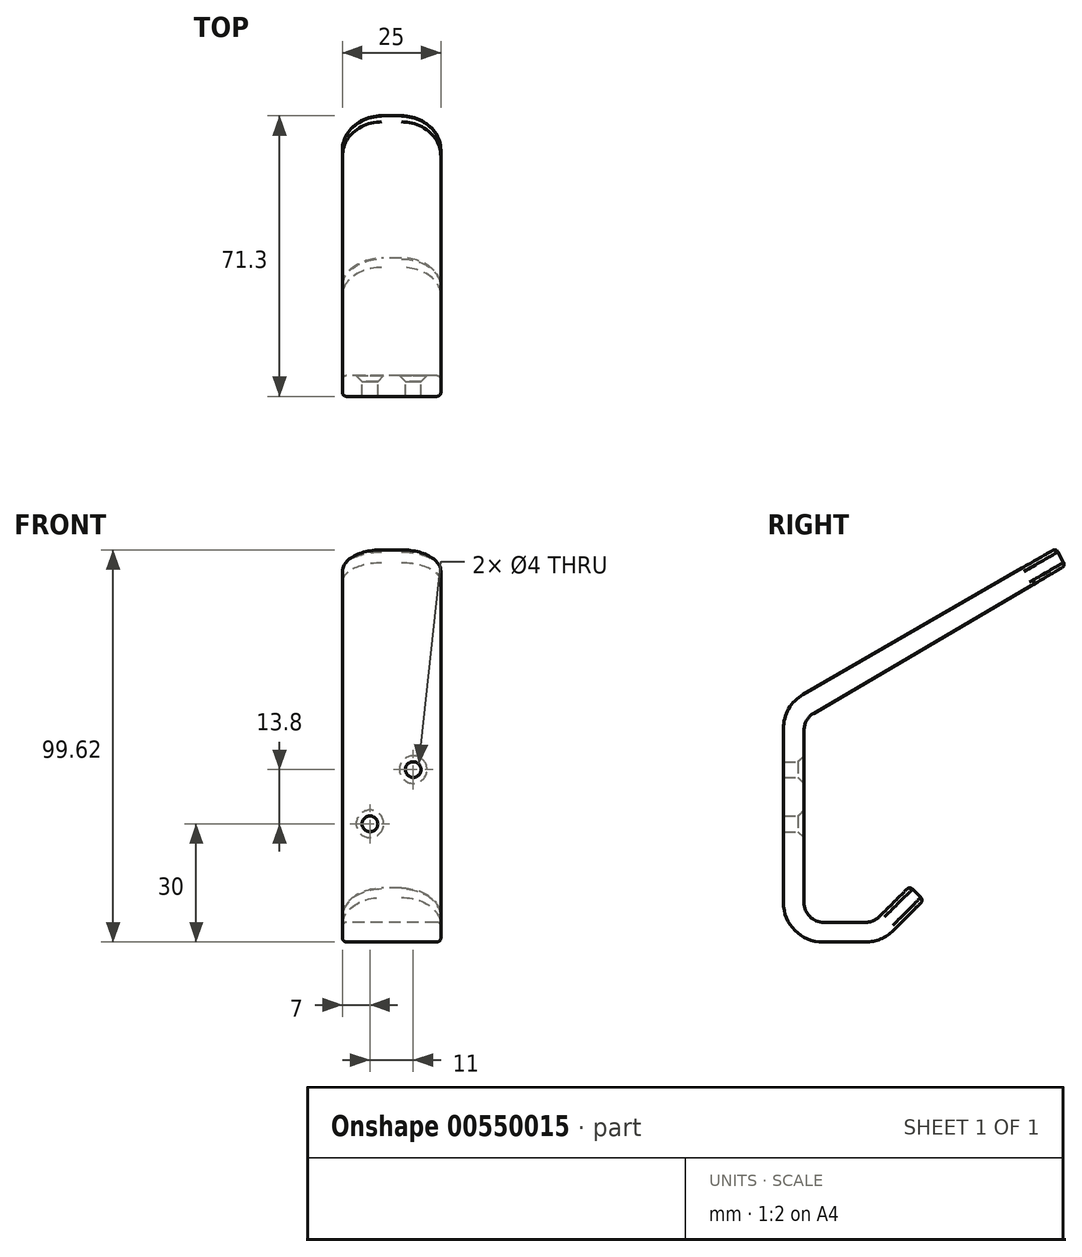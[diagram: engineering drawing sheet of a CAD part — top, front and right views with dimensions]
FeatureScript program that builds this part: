
annotation { "Feature Type Name" : "Feature", "Feature Type Description" : "" }
export const myFeature = defineFeature(function(context is Context, id is Id, definition is map)
    precondition{}
    {
        {
            var Q0;
            Q0=qCreatedBy(makeId("Right.planeOp"),FACE);
            var sketch = newSketch(context, id + "F0", { "sketchPlane" : qUnion([Q0])});
            skLineSegment(sketch, "E0", {"start": v(0, 0) * mm, "end": v(-25, 0) * mm});
            skLineSegment(sketch, "E1", {"start": v(-25, 0) * mm, "end": v(-25, 60) * mm});
            skLineSegment(sketch, "E2", {"start": v(-25, 60) * mm, "end": v(44.28, 100) * mm});
            skLineSegment(sketch, "E3", {"start": v(0, 0) * mm, "end": v(10.6, 10.6) * mm});
            skLineSegment(sketch, "E4", {"start": v(10.6, 10.6) * mm, "end": v(7.07, 14.14) * mm});
            skLineSegment(sketch, "E5", {"start": v(7.07, 14.14) * mm, "end": v(-2.07, 5) * mm});
            skLineSegment(sketch, "E6", {"start": v(-2.07, 5) * mm, "end": v(-19.76, 5) * mm});
            skLineSegment(sketch, "E7", {"start": v(-19.76, 6.6) * mm, "end": v(-19.76, 5) * mm});
            skLineSegment(sketch, "E8", {"start": v(-19.76, 5) * mm, "end": v(-19.76, 56.67) * mm});
            skLineSegment(sketch, "E9", {"start": v(-15.64, 59.09) * mm, "end": v(-19.76, 56.67) * mm});
            skLineSegment(sketch, "E10", {"start": v(-19.76, 56.67) * mm, "end": v(46.64, 95.6) * mm});
            skLineSegment(sketch, "E11", {"start": v(44.28, 100) * mm, "end": v(46.64, 95.6) * mm});
            skSolve(sketch);
        }
        {
            var Q0;
            Q0 = qSketchRegion(id + "F0", true);
            extrude(context, id + "F1", {"entities" : qUnion([Q0]), "depth" : 25 * mm, "offsetDistance" : 25 * mm});
        }
        {
            var Q0;
            Q0=makeQuery(id+"F1.opExtrude","SWEPT_EDGE",EDGE,{"disambiguationData":[OSD([sQuery(id+"F0.wireOp",EDGE,"E8"),sQuery(id+"F0.wireOp",EDGE,"E10")])]});
            var Q1;
            Q1=makeQuery(id+"F1.opExtrude","SWEPT_EDGE",EDGE,{"disambiguationData":[OSD([sQuery(id+"F0.wireOp",EDGE,"E6"),sQuery(id+"F0.wireOp",EDGE,"E8")])]});
            var Q2;
            Q2=makeQuery(id+"F1.opExtrude","SWEPT_EDGE",EDGE,{"disambiguationData":[OSD([sQuery(id+"F0.wireOp",EDGE,"E5"),sQuery(id+"F0.wireOp",EDGE,"E6")])]});
            fillet(context, id + "F2", {"entities" : qUnion([Q0, Q1, Q2]), "radius" : 5 * mm, "tangentPropagation" : true, "allowEdgeOverflow" : false});
        }
        {
            var Q0;
            Q0=makeQuery(id+"F1.opExtrude","SWEPT_EDGE",EDGE,{"disambiguationData":[OSD([sQuery(id+"F0.wireOp",EDGE,"E1"),sQuery(id+"F0.wireOp",EDGE,"E2")])]});
            var Q1;
            Q1=makeQuery(id+"F1.opExtrude","SWEPT_EDGE",EDGE,{"disambiguationData":[OSD([sQuery(id+"F0.wireOp",EDGE,"E0"),sQuery(id+"F0.wireOp",EDGE,"E1")])]});
            var Q2;
            Q2=makeQuery(id+"F1.opExtrude","SWEPT_EDGE",EDGE,{"disambiguationData":[OSD([sQuery(id+"F0.wireOp",EDGE,"E0"),sQuery(id+"F0.wireOp",EDGE,"E3")])]});
            fillet(context, id + "F3", {"entities" : qUnion([Q0, Q1, Q2]), "radius" : 10 * mm, "tangentPropagation" : true, "allowEdgeOverflow" : false});
        }
        {
            var Q0;
            Q0=makeQuery(id+"F1.opExtrude","CAP_EDGE",EDGE,{"disambiguationData":[OSD([sQuery(id+"F0.wireOp",EDGE,"E4")])],"isStart":false});
            var Q1;
            Q1=makeQuery(id+"F1.opExtrude","CAP_EDGE",EDGE,{"disambiguationData":[OSD([sQuery(id+"F0.wireOp",EDGE,"E4")])],"isStart":true});
            fillet(context, id + "F4", {"entities" : qUnion([Q0, Q1]), "radius" : 10 * mm, "tangentPropagation" : true, "allowEdgeOverflow" : false});
        }
        {
            var Q0;
            Q0=makeQuery(id+"F1.opExtrude","CAP_EDGE",EDGE,{"disambiguationData":[OSD([sQuery(id+"F0.wireOp",EDGE,"E11")])],"isStart":false});
            var Q1;
            Q1=makeQuery(id+"F1.opExtrude","CAP_EDGE",EDGE,{"disambiguationData":[OSD([sQuery(id+"F0.wireOp",EDGE,"E11")])],"isStart":true});
            fillet(context, id + "F5", {"entities" : qUnion([Q0, Q1]), "radius" : 10 * mm, "tangentPropagation" : true, "allowEdgeOverflow" : false});
        }
        {
            var Q0;
            Q0=makeQuery(id+"F1.opExtrude","CAP_EDGE",EDGE,{"disambiguationData":[OSD([sQuery(id+"F0.wireOp",EDGE,"E8")])],"isStart":false});
            var Q1;
            Q1=makeQuery(id+"F1.opExtrude","CAP_EDGE",EDGE,{"disambiguationData":[OSD([sQuery(id+"F0.wireOp",EDGE,"E10")])],"isStart":false});
            var Q2;
            {var subQ0=sQuery(id+"F0.wireOp",EDGE,"E10");var subQ1=sQuery(id+"F0.wireOp",EDGE,"E8");Q2=makeQuery(id+"F2.opFillet","BLEND_EDGE",EDGE,{"blendedFrom":[makeQuery(id+"F1.opExtrude","SWEPT_EDGE",EDGE,{"disambiguationData":[OSD([subQ1,subQ0])]}),makeQuery(id+"F1.opExtrude","CAP_FACE",FACE,{"disambiguationData":[OSD([sQuery(id+"F0.wireOp",EDGE,"E0"),sQuery(id+"F0.wireOp",EDGE,"E1"),sQuery(id+"F0.wireOp",EDGE,"E2"),sQuery(id+"F0.wireOp",EDGE,"E3"),sQuery(id+"F0.wireOp",EDGE,"E4"),sQuery(id+"F0.wireOp",EDGE,"E5"),sQuery(id+"F0.wireOp",EDGE,"E6"),subQ1,subQ0,sQuery(id+"F0.wireOp",EDGE,"E11")])],"isStart":false})],"blendedInto":[makeQuery(id+"F1.opExtrude","CAP_FACE",FACE,{"disambiguationData":[OSD([sQuery(id+"F0.wireOp",EDGE,"E0"),sQuery(id+"F0.wireOp",EDGE,"E1"),sQuery(id+"F0.wireOp",EDGE,"E2"),sQuery(id+"F0.wireOp",EDGE,"E3"),sQuery(id+"F0.wireOp",EDGE,"E4"),sQuery(id+"F0.wireOp",EDGE,"E5"),sQuery(id+"F0.wireOp",EDGE,"E6"),subQ1,subQ0,sQuery(id+"F0.wireOp",EDGE,"E11")])],"isStart":false})]});}
            var Q3;
            Q3=makeQuery(id+"F5.opFillet","BLEND_EDGE",EDGE,{"blendedFrom":[makeQuery(id+"F1.opExtrude","CAP_EDGE",EDGE,{"disambiguationData":[OSD([sQuery(id+"F0.wireOp",EDGE,"E11")])],"isStart":false}),makeQuery(id+"F1.opExtrude","SWEPT_FACE",FACE,{"disambiguationData":[OSD([sQuery(id+"F0.wireOp",EDGE,"E10")])]})],"blendedInto":[makeQuery(id+"F1.opExtrude","SWEPT_FACE",FACE,{"disambiguationData":[OSD([sQuery(id+"F0.wireOp",EDGE,"E10")])]})]});
            var Q4;
            Q4=makeQuery(id+"F1.opExtrude","SWEPT_EDGE",EDGE,{"disambiguationData":[OSD([sQuery(id+"F0.wireOp",EDGE,"E10"),sQuery(id+"F0.wireOp",EDGE,"E11")])]});
            var Q5;
            Q5=makeQuery(id+"F5.opFillet","BLEND_EDGE",EDGE,{"blendedFrom":[makeQuery(id+"F1.opExtrude","CAP_EDGE",EDGE,{"disambiguationData":[OSD([sQuery(id+"F0.wireOp",EDGE,"E11")])],"isStart":true}),makeQuery(id+"F1.opExtrude","SWEPT_FACE",FACE,{"disambiguationData":[OSD([sQuery(id+"F0.wireOp",EDGE,"E10")])]})],"blendedInto":[makeQuery(id+"F1.opExtrude","SWEPT_FACE",FACE,{"disambiguationData":[OSD([sQuery(id+"F0.wireOp",EDGE,"E10")])]})]});
            var Q6;
            Q6=makeQuery(id+"F1.opExtrude","CAP_EDGE",EDGE,{"disambiguationData":[OSD([sQuery(id+"F0.wireOp",EDGE,"E10")])],"isStart":true});
            var Q7;
            {var subQ0=sQuery(id+"F0.wireOp",EDGE,"E10");var subQ1=sQuery(id+"F0.wireOp",EDGE,"E8");Q7=makeQuery(id+"F2.opFillet","BLEND_EDGE",EDGE,{"blendedFrom":[makeQuery(id+"F1.opExtrude","SWEPT_EDGE",EDGE,{"disambiguationData":[OSD([subQ1,subQ0])]}),makeQuery(id+"F1.opExtrude","CAP_FACE",FACE,{"disambiguationData":[OSD([sQuery(id+"F0.wireOp",EDGE,"E0"),sQuery(id+"F0.wireOp",EDGE,"E1"),sQuery(id+"F0.wireOp",EDGE,"E2"),sQuery(id+"F0.wireOp",EDGE,"E3"),sQuery(id+"F0.wireOp",EDGE,"E4"),sQuery(id+"F0.wireOp",EDGE,"E5"),sQuery(id+"F0.wireOp",EDGE,"E6"),subQ1,subQ0,sQuery(id+"F0.wireOp",EDGE,"E11")])],"isStart":true})],"blendedInto":[makeQuery(id+"F1.opExtrude","CAP_FACE",FACE,{"disambiguationData":[OSD([sQuery(id+"F0.wireOp",EDGE,"E0"),sQuery(id+"F0.wireOp",EDGE,"E1"),sQuery(id+"F0.wireOp",EDGE,"E2"),sQuery(id+"F0.wireOp",EDGE,"E3"),sQuery(id+"F0.wireOp",EDGE,"E4"),sQuery(id+"F0.wireOp",EDGE,"E5"),sQuery(id+"F0.wireOp",EDGE,"E6"),subQ1,subQ0,sQuery(id+"F0.wireOp",EDGE,"E11")])],"isStart":true})]});}
            var Q8;
            Q8=makeQuery(id+"F1.opExtrude","CAP_EDGE",EDGE,{"disambiguationData":[OSD([sQuery(id+"F0.wireOp",EDGE,"E8")])],"isStart":true});
            fillet(context, id + "F6", {"entities" : qUnion([Q0, Q1, Q2, Q3, Q4, Q5, Q6, Q7, Q8]), "radius" : 1 * mm, "tangentPropagation" : true, "allowEdgeOverflow" : false});
        }
        {
            var Q0;
            Q0=makeQuery(id+"F1.opExtrude","SWEPT_FACE",FACE,{"disambiguationData":[OSD([sQuery(id+"F0.wireOp",EDGE,"E8")])]});
            var sketch = newSketch(context, id + "F7", { "sketchPlane" : qUnion([Q0])});
            skPoint(sketch, "E12", {"position": v(-18, 43.8) * mm});
            skPoint(sketch, "E13", {"position": v(-7, 30) * mm});
            skSolve(sketch);
        }
        {
            var Q0;
            Q0=sQuery(id+"F7.wireOp",VERTEX,"E12");
            var Q1;
            Q1=sQuery(id+"F7.wireOp",VERTEX,"E13");
            var Q2;
            Q2=makeQuery(id+"F1.opExtrude","SWEPT_BODY",BODY,{"disambiguationData":[OSD([sQuery(id+"F0.wireOp",EDGE,"E0"),sQuery(id+"F0.wireOp",EDGE,"E1"),sQuery(id+"F0.wireOp",EDGE,"E2"),sQuery(id+"F0.wireOp",EDGE,"E3"),sQuery(id+"F0.wireOp",EDGE,"E4"),sQuery(id+"F0.wireOp",EDGE,"E5"),sQuery(id+"F0.wireOp",EDGE,"E6"),sQuery(id+"F0.wireOp",EDGE,"E8"),sQuery(id+"F0.wireOp",EDGE,"E10"),sQuery(id+"F0.wireOp",EDGE,"E11")])]});
            hole(context, id + "F8", {"style" : HoleStyle.C_SINK, "endStyle" : HoleEndStyle.THROUGH, "holeDiameter" : 4 * mm, "cSinkDiameter" : 7 * mm, "cSinkAngle" : 90 * degree, "isTappedThrough" : true, "tappedDepth" : 12 * mm, "tapClearance" : 3, "locations" : qUnion([Q0, Q1]), "scope" : qUnion([Q2])});
        }
        {
            var Q0;
            Q0=makeQuery(id+"F4.opFillet","BLEND_EDGE",EDGE,{"blendedFrom":[makeQuery(id+"F1.opExtrude","CAP_EDGE",EDGE,{"disambiguationData":[OSD([sQuery(id+"F0.wireOp",EDGE,"E4")])],"isStart":false}),makeQuery(id+"F1.opExtrude","SWEPT_FACE",FACE,{"disambiguationData":[OSD([sQuery(id+"F0.wireOp",EDGE,"E3")])]})],"blendedInto":[makeQuery(id+"F1.opExtrude","SWEPT_FACE",FACE,{"disambiguationData":[OSD([sQuery(id+"F0.wireOp",EDGE,"E3")])]})]});
            var Q1;
            Q1=makeQuery(id+"F1.opExtrude","SWEPT_EDGE",EDGE,{"disambiguationData":[OSD([sQuery(id+"F0.wireOp",EDGE,"E3"),sQuery(id+"F0.wireOp",EDGE,"E4")])]});
            var Q2;
            Q2=makeQuery(id+"F4.opFillet","BLEND_EDGE",EDGE,{"blendedFrom":[makeQuery(id+"F1.opExtrude","CAP_EDGE",EDGE,{"disambiguationData":[OSD([sQuery(id+"F0.wireOp",EDGE,"E4")])],"isStart":true}),makeQuery(id+"F1.opExtrude","SWEPT_FACE",FACE,{"disambiguationData":[OSD([sQuery(id+"F0.wireOp",EDGE,"E3")])]})],"blendedInto":[makeQuery(id+"F1.opExtrude","SWEPT_FACE",FACE,{"disambiguationData":[OSD([sQuery(id+"F0.wireOp",EDGE,"E3")])]})]});
            var Q3;
            {var subQ0=sQuery(id+"F0.wireOp",EDGE,"E3");var subQ1=sQuery(id+"F0.wireOp",EDGE,"E0");Q3=makeQuery(id+"F3.opFillet","BLEND_EDGE",EDGE,{"blendedFrom":[makeQuery(id+"F1.opExtrude","SWEPT_EDGE",EDGE,{"disambiguationData":[OSD([subQ1,subQ0])]}),makeQuery(id+"F1.opExtrude","CAP_FACE",FACE,{"disambiguationData":[OSD([subQ1,sQuery(id+"F0.wireOp",EDGE,"E1"),sQuery(id+"F0.wireOp",EDGE,"E2"),subQ0,sQuery(id+"F0.wireOp",EDGE,"E4"),sQuery(id+"F0.wireOp",EDGE,"E5"),sQuery(id+"F0.wireOp",EDGE,"E6"),sQuery(id+"F0.wireOp",EDGE,"E8"),sQuery(id+"F0.wireOp",EDGE,"E10"),sQuery(id+"F0.wireOp",EDGE,"E11")])],"isStart":true})],"blendedInto":[makeQuery(id+"F1.opExtrude","CAP_FACE",FACE,{"disambiguationData":[OSD([subQ1,sQuery(id+"F0.wireOp",EDGE,"E1"),sQuery(id+"F0.wireOp",EDGE,"E2"),subQ0,sQuery(id+"F0.wireOp",EDGE,"E4"),sQuery(id+"F0.wireOp",EDGE,"E5"),sQuery(id+"F0.wireOp",EDGE,"E6"),sQuery(id+"F0.wireOp",EDGE,"E8"),sQuery(id+"F0.wireOp",EDGE,"E10"),sQuery(id+"F0.wireOp",EDGE,"E11")])],"isStart":true})]});}
            var Q4;
            Q4=makeQuery(id+"F1.opExtrude","CAP_EDGE",EDGE,{"disambiguationData":[OSD([sQuery(id+"F0.wireOp",EDGE,"E3")])],"isStart":true});
            var Q5;
            Q5=makeQuery(id+"F1.opExtrude","CAP_EDGE",EDGE,{"disambiguationData":[OSD([sQuery(id+"F0.wireOp",EDGE,"E0")])],"isStart":true});
            var Q6;
            {var subQ0=sQuery(id+"F0.wireOp",EDGE,"E3");var subQ1=sQuery(id+"F0.wireOp",EDGE,"E0");Q6=makeQuery(id+"F3.opFillet","BLEND_EDGE",EDGE,{"blendedFrom":[makeQuery(id+"F1.opExtrude","SWEPT_EDGE",EDGE,{"disambiguationData":[OSD([subQ1,subQ0])]}),makeQuery(id+"F1.opExtrude","CAP_FACE",FACE,{"disambiguationData":[OSD([subQ1,sQuery(id+"F0.wireOp",EDGE,"E1"),sQuery(id+"F0.wireOp",EDGE,"E2"),subQ0,sQuery(id+"F0.wireOp",EDGE,"E4"),sQuery(id+"F0.wireOp",EDGE,"E5"),sQuery(id+"F0.wireOp",EDGE,"E6"),sQuery(id+"F0.wireOp",EDGE,"E8"),sQuery(id+"F0.wireOp",EDGE,"E10"),sQuery(id+"F0.wireOp",EDGE,"E11")])],"isStart":false})],"blendedInto":[makeQuery(id+"F1.opExtrude","CAP_FACE",FACE,{"disambiguationData":[OSD([subQ1,sQuery(id+"F0.wireOp",EDGE,"E1"),sQuery(id+"F0.wireOp",EDGE,"E2"),subQ0,sQuery(id+"F0.wireOp",EDGE,"E4"),sQuery(id+"F0.wireOp",EDGE,"E5"),sQuery(id+"F0.wireOp",EDGE,"E6"),sQuery(id+"F0.wireOp",EDGE,"E8"),sQuery(id+"F0.wireOp",EDGE,"E10"),sQuery(id+"F0.wireOp",EDGE,"E11")])],"isStart":false})]});}
            var Q7;
            Q7=makeQuery(id+"F1.opExtrude","CAP_EDGE",EDGE,{"disambiguationData":[OSD([sQuery(id+"F0.wireOp",EDGE,"E3")])],"isStart":false});
            var Q8;
            Q8=makeQuery(id+"F1.opExtrude","CAP_EDGE",EDGE,{"disambiguationData":[OSD([sQuery(id+"F0.wireOp",EDGE,"E0")])],"isStart":false});
            var Q9;
            {var subQ0=sQuery(id+"F0.wireOp",EDGE,"E1");var subQ1=sQuery(id+"F0.wireOp",EDGE,"E0");Q9=makeQuery(id+"F3.opFillet","BLEND_EDGE",EDGE,{"blendedFrom":[makeQuery(id+"F1.opExtrude","SWEPT_EDGE",EDGE,{"disambiguationData":[OSD([subQ1,subQ0])]}),makeQuery(id+"F1.opExtrude","CAP_FACE",FACE,{"disambiguationData":[OSD([subQ1,subQ0,sQuery(id+"F0.wireOp",EDGE,"E2"),sQuery(id+"F0.wireOp",EDGE,"E3"),sQuery(id+"F0.wireOp",EDGE,"E4"),sQuery(id+"F0.wireOp",EDGE,"E5"),sQuery(id+"F0.wireOp",EDGE,"E6"),sQuery(id+"F0.wireOp",EDGE,"E8"),sQuery(id+"F0.wireOp",EDGE,"E10"),sQuery(id+"F0.wireOp",EDGE,"E11")])],"isStart":false})],"blendedInto":[makeQuery(id+"F1.opExtrude","CAP_FACE",FACE,{"disambiguationData":[OSD([subQ1,subQ0,sQuery(id+"F0.wireOp",EDGE,"E2"),sQuery(id+"F0.wireOp",EDGE,"E3"),sQuery(id+"F0.wireOp",EDGE,"E4"),sQuery(id+"F0.wireOp",EDGE,"E5"),sQuery(id+"F0.wireOp",EDGE,"E6"),sQuery(id+"F0.wireOp",EDGE,"E8"),sQuery(id+"F0.wireOp",EDGE,"E10"),sQuery(id+"F0.wireOp",EDGE,"E11")])],"isStart":false})]});}
            var Q10;
            {var subQ0=sQuery(id+"F0.wireOp",EDGE,"E1");var subQ1=sQuery(id+"F0.wireOp",EDGE,"E0");Q10=makeQuery(id+"F3.opFillet","BLEND_EDGE",EDGE,{"blendedFrom":[makeQuery(id+"F1.opExtrude","SWEPT_EDGE",EDGE,{"disambiguationData":[OSD([subQ1,subQ0])]}),makeQuery(id+"F1.opExtrude","CAP_FACE",FACE,{"disambiguationData":[OSD([subQ1,subQ0,sQuery(id+"F0.wireOp",EDGE,"E2"),sQuery(id+"F0.wireOp",EDGE,"E3"),sQuery(id+"F0.wireOp",EDGE,"E4"),sQuery(id+"F0.wireOp",EDGE,"E5"),sQuery(id+"F0.wireOp",EDGE,"E6"),sQuery(id+"F0.wireOp",EDGE,"E8"),sQuery(id+"F0.wireOp",EDGE,"E10"),sQuery(id+"F0.wireOp",EDGE,"E11")])],"isStart":true})],"blendedInto":[makeQuery(id+"F1.opExtrude","CAP_FACE",FACE,{"disambiguationData":[OSD([subQ1,subQ0,sQuery(id+"F0.wireOp",EDGE,"E2"),sQuery(id+"F0.wireOp",EDGE,"E3"),sQuery(id+"F0.wireOp",EDGE,"E4"),sQuery(id+"F0.wireOp",EDGE,"E5"),sQuery(id+"F0.wireOp",EDGE,"E6"),sQuery(id+"F0.wireOp",EDGE,"E8"),sQuery(id+"F0.wireOp",EDGE,"E10"),sQuery(id+"F0.wireOp",EDGE,"E11")])],"isStart":true})]});}
            var Q11;
            Q11=makeQuery(id+"F1.opExtrude","CAP_EDGE",EDGE,{"disambiguationData":[OSD([sQuery(id+"F0.wireOp",EDGE,"E1")])],"isStart":false});
            var Q12;
            Q12=makeQuery(id+"F1.opExtrude","CAP_EDGE",EDGE,{"disambiguationData":[OSD([sQuery(id+"F0.wireOp",EDGE,"E1")])],"isStart":true});
            var Q13;
            {var subQ0=sQuery(id+"F0.wireOp",EDGE,"E2");var subQ1=sQuery(id+"F0.wireOp",EDGE,"E1");Q13=makeQuery(id+"F3.opFillet","BLEND_EDGE",EDGE,{"blendedFrom":[makeQuery(id+"F1.opExtrude","SWEPT_EDGE",EDGE,{"disambiguationData":[OSD([subQ1,subQ0])]}),makeQuery(id+"F1.opExtrude","CAP_FACE",FACE,{"disambiguationData":[OSD([sQuery(id+"F0.wireOp",EDGE,"E0"),subQ1,subQ0,sQuery(id+"F0.wireOp",EDGE,"E3"),sQuery(id+"F0.wireOp",EDGE,"E4"),sQuery(id+"F0.wireOp",EDGE,"E5"),sQuery(id+"F0.wireOp",EDGE,"E6"),sQuery(id+"F0.wireOp",EDGE,"E8"),sQuery(id+"F0.wireOp",EDGE,"E10"),sQuery(id+"F0.wireOp",EDGE,"E11")])],"isStart":false})],"blendedInto":[makeQuery(id+"F1.opExtrude","CAP_FACE",FACE,{"disambiguationData":[OSD([sQuery(id+"F0.wireOp",EDGE,"E0"),subQ1,subQ0,sQuery(id+"F0.wireOp",EDGE,"E3"),sQuery(id+"F0.wireOp",EDGE,"E4"),sQuery(id+"F0.wireOp",EDGE,"E5"),sQuery(id+"F0.wireOp",EDGE,"E6"),sQuery(id+"F0.wireOp",EDGE,"E8"),sQuery(id+"F0.wireOp",EDGE,"E10"),sQuery(id+"F0.wireOp",EDGE,"E11")])],"isStart":false})]});}
            var Q14;
            Q14=makeQuery(id+"F1.opExtrude","CAP_EDGE",EDGE,{"disambiguationData":[OSD([sQuery(id+"F0.wireOp",EDGE,"E2")])],"isStart":false});
            var Q15;
            {var subQ0=sQuery(id+"F0.wireOp",EDGE,"E2");var subQ1=sQuery(id+"F0.wireOp",EDGE,"E1");Q15=makeQuery(id+"F3.opFillet","BLEND_EDGE",EDGE,{"blendedFrom":[makeQuery(id+"F1.opExtrude","SWEPT_EDGE",EDGE,{"disambiguationData":[OSD([subQ1,subQ0])]}),makeQuery(id+"F1.opExtrude","CAP_FACE",FACE,{"disambiguationData":[OSD([sQuery(id+"F0.wireOp",EDGE,"E0"),subQ1,subQ0,sQuery(id+"F0.wireOp",EDGE,"E3"),sQuery(id+"F0.wireOp",EDGE,"E4"),sQuery(id+"F0.wireOp",EDGE,"E5"),sQuery(id+"F0.wireOp",EDGE,"E6"),sQuery(id+"F0.wireOp",EDGE,"E8"),sQuery(id+"F0.wireOp",EDGE,"E10"),sQuery(id+"F0.wireOp",EDGE,"E11")])],"isStart":true})],"blendedInto":[makeQuery(id+"F1.opExtrude","CAP_FACE",FACE,{"disambiguationData":[OSD([sQuery(id+"F0.wireOp",EDGE,"E0"),subQ1,subQ0,sQuery(id+"F0.wireOp",EDGE,"E3"),sQuery(id+"F0.wireOp",EDGE,"E4"),sQuery(id+"F0.wireOp",EDGE,"E5"),sQuery(id+"F0.wireOp",EDGE,"E6"),sQuery(id+"F0.wireOp",EDGE,"E8"),sQuery(id+"F0.wireOp",EDGE,"E10"),sQuery(id+"F0.wireOp",EDGE,"E11")])],"isStart":true})]});}
            var Q16;
            Q16=makeQuery(id+"F1.opExtrude","CAP_EDGE",EDGE,{"disambiguationData":[OSD([sQuery(id+"F0.wireOp",EDGE,"E2")])],"isStart":true});
            var Q17;
            Q17=makeQuery(id+"F5.opFillet","BLEND_EDGE",EDGE,{"blendedFrom":[makeQuery(id+"F1.opExtrude","CAP_EDGE",EDGE,{"disambiguationData":[OSD([sQuery(id+"F0.wireOp",EDGE,"E11")])],"isStart":false}),makeQuery(id+"F1.opExtrude","SWEPT_FACE",FACE,{"disambiguationData":[OSD([sQuery(id+"F0.wireOp",EDGE,"E2")])]})],"blendedInto":[makeQuery(id+"F1.opExtrude","SWEPT_FACE",FACE,{"disambiguationData":[OSD([sQuery(id+"F0.wireOp",EDGE,"E2")])]})]});
            var Q18;
            Q18=makeQuery(id+"F5.opFillet","BLEND_EDGE",EDGE,{"blendedFrom":[makeQuery(id+"F1.opExtrude","CAP_EDGE",EDGE,{"disambiguationData":[OSD([sQuery(id+"F0.wireOp",EDGE,"E11")])],"isStart":true}),makeQuery(id+"F1.opExtrude","SWEPT_FACE",FACE,{"disambiguationData":[OSD([sQuery(id+"F0.wireOp",EDGE,"E2")])]})],"blendedInto":[makeQuery(id+"F1.opExtrude","SWEPT_FACE",FACE,{"disambiguationData":[OSD([sQuery(id+"F0.wireOp",EDGE,"E2")])]})]});
            var Q19;
            Q19=makeQuery(id+"F1.opExtrude","SWEPT_EDGE",EDGE,{"disambiguationData":[OSD([sQuery(id+"F0.wireOp",EDGE,"E2"),sQuery(id+"F0.wireOp",EDGE,"E11")])]});
            fillet(context, id + "F9", {"entities" : qUnion([Q0, Q1, Q2, Q3, Q4, Q5, Q6, Q7, Q8, Q9, Q10, Q11, Q12, Q13, Q14, Q15, Q16, Q17, Q18, Q19]), "radius" : 1 * mm, "tangentPropagation" : true, "allowEdgeOverflow" : false});
        }
    });
